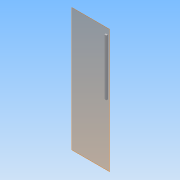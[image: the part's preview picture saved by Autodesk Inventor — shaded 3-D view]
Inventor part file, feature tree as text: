
AUTODESK INVENTOR PART (.ipt)
format: ipt  version: 2013 (Build 170138000, 138)  size: 78,336 bytes
history: native  units: in
note: dims shown in document units (in); Inventor stores cm internally (conversion verified against a paired STEP export)
features: extrude x2, sketch x2, plane x1
ambient origin geometry x8: Origin, YZ Plane, XZ Plane, XY Plane, X Axis, Y Axis, Z Axis, Center Point
bodies: Solid1 (feature_tree)
feature tree (5):
  plane  "Work Plane1"
  extrude  "Extrusion1"  Depth=1.5in
  extrude  "Extrusion2"  TaperAngle=0.0deg  [1 undecoded]
  sketch  "Sketch1"  dims[d0=39.0in d2=1.5in]
  sketch  "Sketch2"  dims[d3=1.0in d4=0.0in d5=38.5in d7=0.5in d8=0.3332in d9=0.0in]
note: 1 required parameter value undecoded (feature->parameter linkage not recoverable at this tier; creation-order binding heuristic only, values carry confidence <= 0.55)
